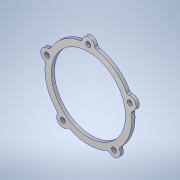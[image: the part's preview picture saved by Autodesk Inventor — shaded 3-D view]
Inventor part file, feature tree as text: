
AUTODESK INVENTOR PART (.ipt)
format: ipt  version: 2020 (Build 240168000, 168)  size: 168,448 bytes
history: native  units: mm
features: extrude x2, sketch x2, other x1, fillet x1, projected_geometry x1
ambient origin geometry x8: Origin, YZ Plane, XZ Plane, XY Plane, X Axis, Y Axis, Z Axis, Center Point
bodies: Body1 (feature_tree)
feature tree (7):
  other  "솔리드1"
  extrude  "돌출1"  Depth=47.07mm
  extrude  "돌출2"  Depth=55.2mm
  fillet  "모깎기1"  Radius=8.0mm
  sketch  "스케치1"
  sketch  "스케치2"
  projected_geometry  "투영된 루프1"
